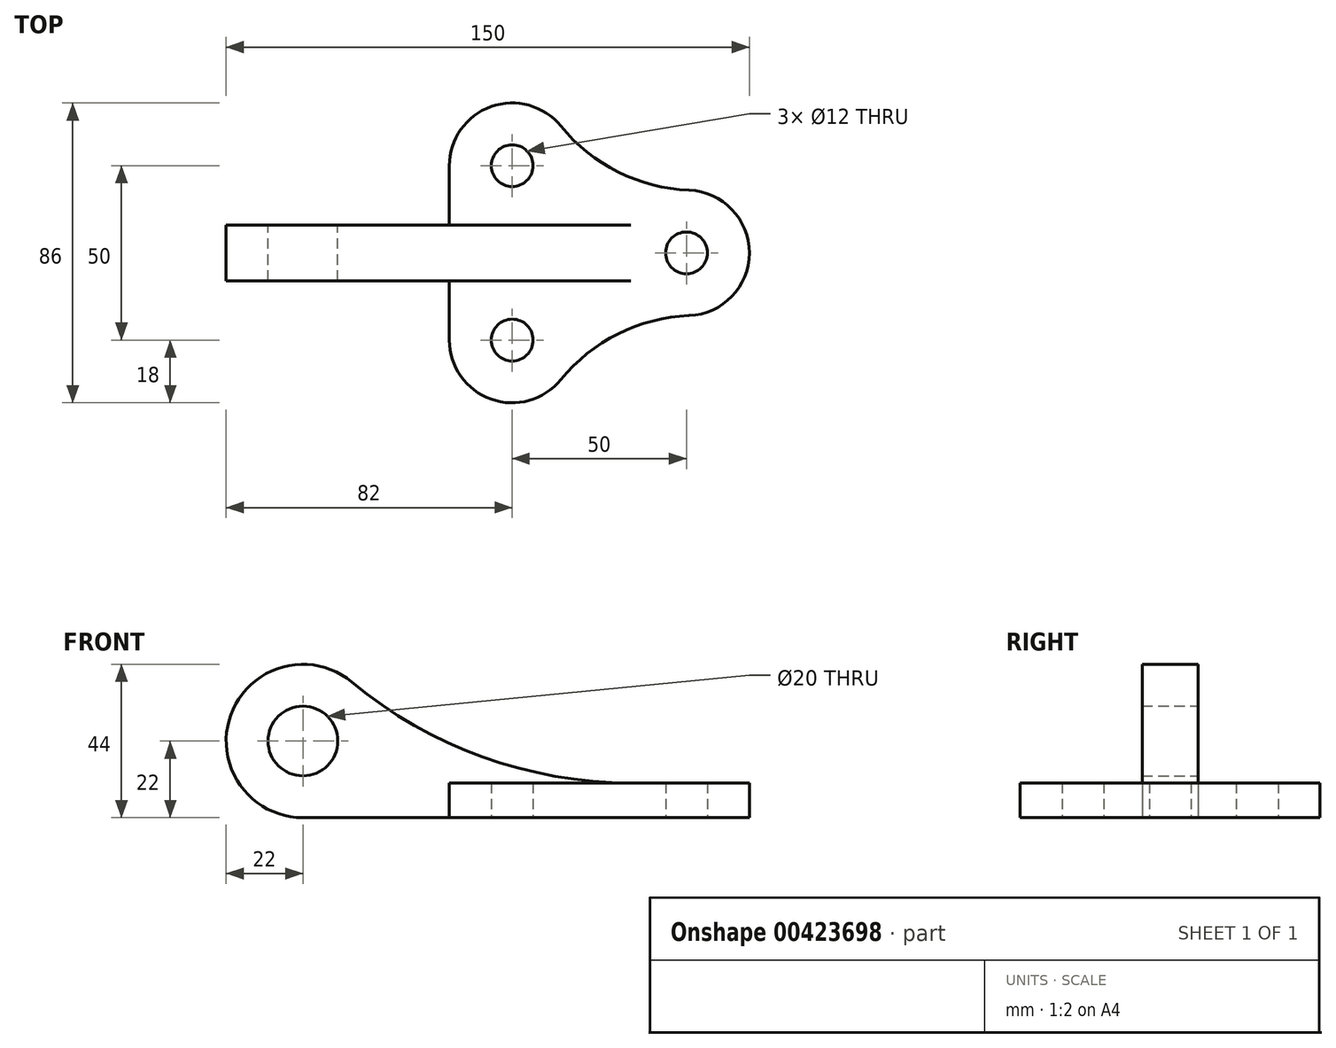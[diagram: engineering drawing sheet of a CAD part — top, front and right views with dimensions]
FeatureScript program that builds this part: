
annotation { "Feature Type Name" : "Feature", "Feature Type Description" : "" }
export const myFeature = defineFeature(function(context is Context, id is Id, definition is map)
    precondition{}
    {
        {
            var Q0;
            Q0=qCreatedBy(makeId("Top.planeOp"),FACE);
            var sketch = newSketch(context, id + "F0", { "sketchPlane" : qUnion([Q0])});
            skArc(sketch, "E0", {"start": v(13.96, 36.37) * mm, "mid": v(-6.03, 41.96) * mm, "end": v(-18, 25) * mm});
            skArc(sketch, "E1", {"start": v(-18, -25) * mm, "mid": v(-6.03, -41.96) * mm, "end": v(13.96, -36.37) * mm});
            skArc(sketch, "E2", {"start": v(50.72, -17.99) * mm, "mid": v(68, 0) * mm, "end": v(50.72, 17.99) * mm});
            skArc(sketch, "E3", {"start": v(13.96, 36.37) * mm, "mid": v(30.36, 23.22) * mm, "end": v(50.72, 17.99) * mm});
            skArc(sketch, "E4.MirrorCS", {"start": v(13.96, -36.37) * mm, "mid": v(30.36, -23.22) * mm, "end": v(50.72, -17.99) * mm});
            skLineSegment(sketch, "E5", {"start": v(-18, 25) * mm, "end": v(-18, -25) * mm});
            skCircle(sketch, "E6", {"center": v(0, 25) * mm, "radius": 6 * mm});
            skCircle(sketch, "E7", {"center": v(0, -25) * mm, "radius": 6 * mm});
            skCircle(sketch, "E8", {"center": v(50, 0) * mm, "radius": 6 * mm});
            skSolve(sketch);
        }
        {
            var Q0;
            Q0=makeQuery(id+"F0.imprint","IMPRINT",FACE,{"disambiguationData":[TD([[makeQuery(id+"F0.imprint","IMPRINT",EDGE,{"derivedFrom":sQuery(id+"F0.wireOp",EDGE,"E0")}),1.0]])]});
            extrude(context, id + "F1", {"entities" : qUnion([Q0]), "depth" : 10 * mm});
        }
        {
            var Q0;
            Q0=qCreatedBy(makeId("Front.planeOp"),FACE);
            var sketch = newSketch(context, id + "F2", { "sketchPlane" : qUnion([Q0])});
            skArc(sketch, "E9", {"start": v(-45.93, 38.91) * mm, "mid": v(-80.69, 29.48) * mm, "end": v(-60, 0) * mm});
            skLineSegment(sketch, "E10.0", {"start": v(34.02, 10) * mm, "end": v(50.72, 10) * mm});
            skArc(sketch, "E11", {"start": v(-45.93, 38.91) * mm, "mid": v(-8.49, 17.45) * mm, "end": v(34.02, 10) * mm});
            skLineSegment(sketch, "E12", {"start": v(26.77, 0) * mm, "end": v(-129.7, 0) * mm});
            skLineSegment(sketch, "E13.0", {"start": v(44, 0) * mm, "end": v(56, 0) * mm});
            skLineSegment(sketch, "E14", {"start": v(44, 0) * mm, "end": v(44, 10) * mm});
            skLineSegment(sketch, "E15", {"start": v(56, 10) * mm, "end": v(56, 0) * mm});
            skPoint(sketch, "E16.0.start.orphan", {"position": v(-18, 10) * mm});
            skPoint(sketch, "E17.orphan", {"position": v(13.96, 10) * mm});
            skLineSegment(sketch, "E18", {"start": v(34.02, 10) * mm, "end": v(26.77, 0) * mm});
            skCircle(sketch, "E19", {"center": v(-60, 22) * mm, "radius": 10 * mm});
            skSolve(sketch);
        }
        {
            var Q0;
            {var subQ0=sQuery(id+"F2.wireOp",EDGE,"E9");Q0=makeQuery(id+"F2.imprint","IMPRINT",FACE,{"disambiguationData":[TD([[makeQuery(id+"F2.imprint","IMPRINT",EDGE,{"derivedFrom":subQ0}),1.0]])]});}
            extrude(context, id + "F3", {"entities" : qUnion([Q0]), "operationType" : NewBodyOperationType.ADD, "endBound" : BoundingType.SYMMETRIC, "depth" : 16 * mm});
        }
    });
